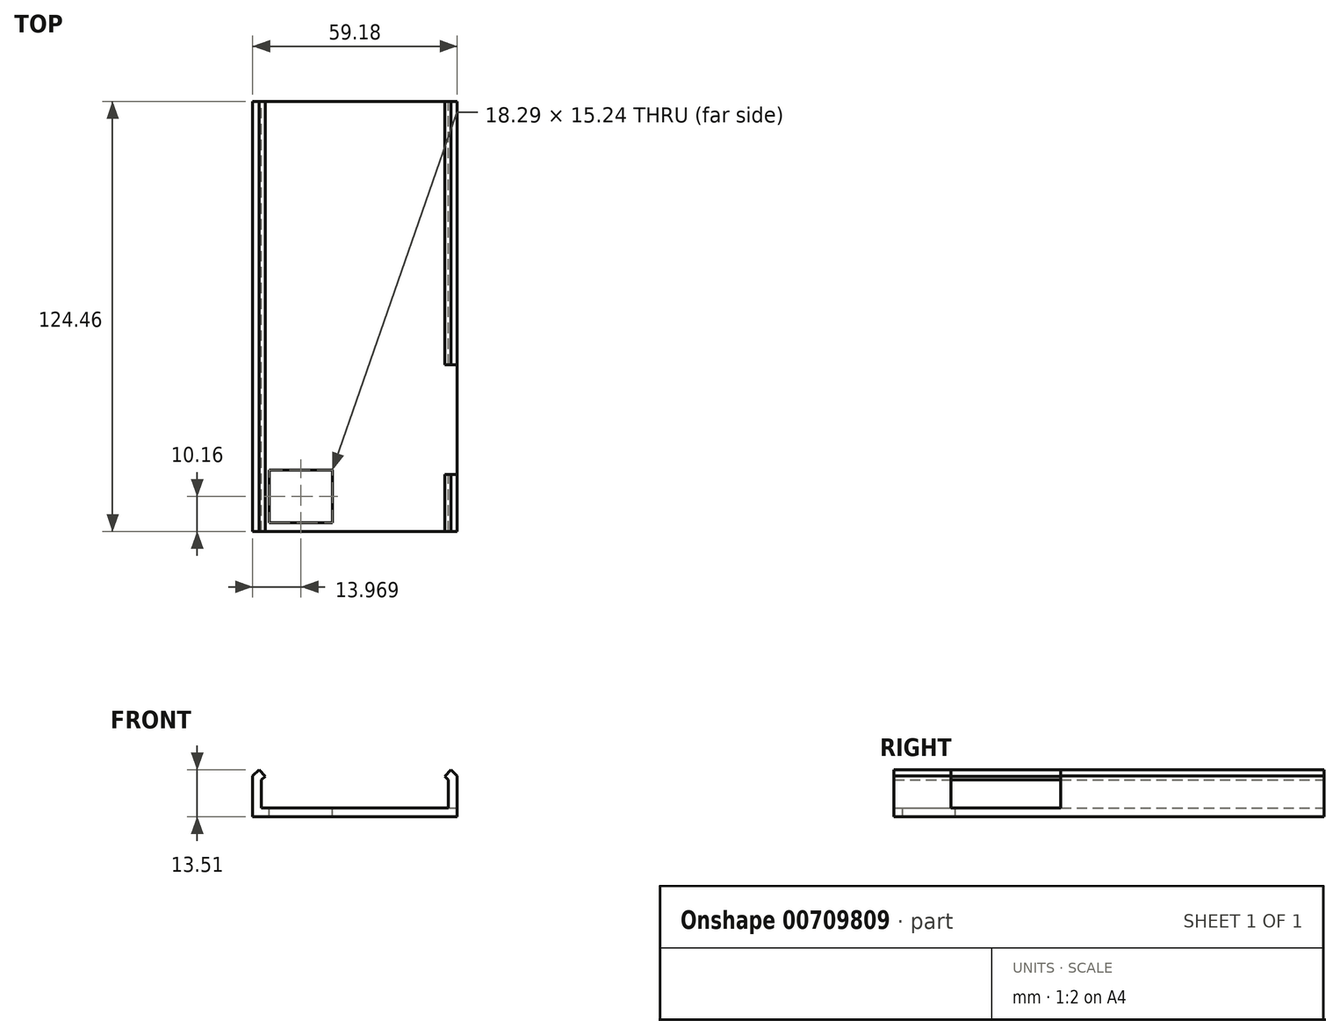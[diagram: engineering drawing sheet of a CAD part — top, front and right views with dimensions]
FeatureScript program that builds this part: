
annotation { "Feature Type Name" : "Feature", "Feature Type Description" : "" }
export const myFeature = defineFeature(function(context is Context, id is Id, definition is map)
    precondition{}
    {
        {
            var Q0;
            Q0=qCreatedBy(makeId("Front.planeOp"),FACE);
            var sketch = newSketch(context, id + "F0", { "sketchPlane" : qUnion([Q0])});
            skLineSegment(sketch, "E0", {"start": v(0, 0) * mm, "end": v(29.6, 0) * mm});
            skLineSegment(sketch, "E1", {"start": v(29.6, 0) * mm, "end": v(29.6, 11.74) * mm});
            skLineSegment(sketch, "E2", {"start": v(29.6, 11.74) * mm, "end": v(27.77, 13.51) * mm});
            skLineSegment(sketch, "E3.MirrorCS", {"start": v(0, 0) * mm, "end": v(-29.6, 0) * mm});
            skLineSegment(sketch, "E4.MirrorCS", {"start": v(-29.6, 0) * mm, "end": v(-29.6, 11.74) * mm});
            skLineSegment(sketch, "E5.MirrorCS", {"start": v(-29.6, 11.74) * mm, "end": v(-27.77, 13.51) * mm});
            skLineSegment(sketch, "E6.0", {"start": v(0, 2.54) * mm, "end": v(-27.05, 2.54) * mm});
            skLineSegment(sketch, "E7.0", {"start": v(-27.05, 2.54) * mm, "end": v(-27.05, 10.67) * mm});
            skLineSegment(sketch, "E8.0", {"start": v(-27.05, 10.67) * mm, "end": v(-26, 11.7) * mm});
            skLineSegment(sketch, "E9", {"start": v(-26, 11.7) * mm, "end": v(-27.77, 13.51) * mm});
            skLineSegment(sketch, "E10.MirrorCS", {"start": v(0, 2.54) * mm, "end": v(27.05, 2.54) * mm});
            skLineSegment(sketch, "E11.MirrorCS", {"start": v(27.05, 10.67) * mm, "end": v(26, 11.7) * mm});
            skLineSegment(sketch, "E12.MirrorCS", {"start": v(27.05, 2.54) * mm, "end": v(27.05, 10.67) * mm});
            skLineSegment(sketch, "E13.MirrorCS", {"start": v(26, 11.7) * mm, "end": v(27.77, 13.51) * mm});
            skSolve(sketch);
        }
        {
            var Q0;
            Q0 = qSketchRegion(id + "F0", true);
            extrude(context, id + "F1", {"entities" : qUnion([Q0]), "depth" : 124.46 * mm, "offsetDistance" : 25.4 * mm});
        }
        {
            var Q0;
            Q0=makeQuery(id+"F1.opExtrude","SWEPT_FACE",FACE,{"disambiguationData":[OSD([sQuery(id+"F0.wireOp",EDGE,"E1")])]});
            var sketch = newSketch(context, id + "F2", { "sketchPlane" : qUnion([Q0])});
            skLineSegment(sketch, "E14.bottom", {"start": v(-76.2, 27.21) * mm, "end": v(-107.95, 27.21) * mm});
            skLineSegment(sketch, "E14.top", {"start": v(-76.2, 2.54) * mm, "end": v(-107.95, 2.54) * mm});
            skLineSegment(sketch, "E14.left", {"start": v(-76.2, 27.21) * mm, "end": v(-76.2, 2.54) * mm});
            skLineSegment(sketch, "E14.right", {"start": v(-107.95, 27.21) * mm, "end": v(-107.95, 2.54) * mm});
            skSolve(sketch);
        }
        {
            var Q0;
            Q0 = qSketchRegion(id + "F2", true);
            extrude(context, id + "F3", {"entities" : qUnion([Q0]), "operationType" : NewBodyOperationType.REMOVE, "oppositeDirection" : true, "depth" : 8.64 * mm, "offsetDistance" : 25.4 * mm});
        }
        {
            var Q0;
            Q0=makeQuery(id+"F3.boolean.opBoolean","MERGE",FACE,{"derivedFrom":[makeQuery(id+"F1.opExtrude","SWEPT_FACE",FACE,{"disambiguationData":[OSD([sQuery(id+"F0.wireOp",EDGE,"E6.0"),sQuery(id+"F0.wireOp",EDGE,"E10.MirrorCS")])]}),makeQuery(id+"F3.opExtrude","SWEPT_FACE",FACE,{"disambiguationData":[OSD([sQuery(id+"F2.wireOp",EDGE,"E14.top")])]})]});
            var sketch = newSketch(context, id + "F4", { "sketchPlane" : qUnion([Q0])});
            skLineSegment(sketch, "E15.bottom", {"start": v(-24.77, -121.92) * mm, "end": v(-6.48, -121.92) * mm});
            skLineSegment(sketch, "E15.top", {"start": v(-24.77, -106.68) * mm, "end": v(-6.48, -106.68) * mm});
            skLineSegment(sketch, "E15.left", {"start": v(-24.77, -121.92) * mm, "end": v(-24.77, -106.68) * mm});
            skLineSegment(sketch, "E15.right", {"start": v(-6.48, -121.92) * mm, "end": v(-6.48, -106.68) * mm});
            skSolve(sketch);
        }
        {
            var Q0;
            Q0 = qSketchRegion(id + "F4", true);
            extrude(context, id + "F5", {"entities" : qUnion([Q0]), "operationType" : NewBodyOperationType.REMOVE, "endBound" : BoundingType.THROUGH_ALL, "oppositeDirection" : true, "depth" : 25.4 * mm, "offsetDistance" : 25.4 * mm});
        }
    });
